# Revit family: for update_71130XXX_new
name_source: partatom
category: Plumbing Fixtures
revit_build: Autodesk Revit 2018 (Build: 20170223_1515(x64)
units: mm (PartAtom-declared; Revit-internal decimal feet)

## family parameters
Always vertical = No
Cut with Voids When Loaded = No
OmniClass Number = 23.31.11.00
OmniClass Title = Faucets
Part Type = Normal
Room Calculation Point = No
Round Connector Dimension = Use Diameter
Shared = No
Work Plane-Based = Yes

## types (1)
- 670 Matte Black
    Always visible = Yes
    BIMobject category = Taps & Mixers
    Connector Description = Water Inlet 9.5mm
    Default Elevation = 1219.2 mm  [stored 4 ft]
    Description = Logis Single lever basin mixer 210 with swivel spout and pop-up waste set
    Design country = Germany
    Diameter = 10 mm
    Edition number = 1
    IFC Classification = Valve
    Manufacturer = Hansgrohe
    Manufacturer country = Germany
    Manufacturer name = hansgrohe
    Masterformat 2014 Code = 22 41 39
    Masterformat 2014 Description = Residential Faucets, Supplies, and Trim
    Material 1 = Hansgrohe - Metal - 670 Matte Black
    Model = 71130XXX
    OmniClass Code = 23-31 11 00
    OmniClass Description = Faucets
    Product Guid = 0d3ea6d5-0a21-4000-b140-4378dfaab38f
    Product SKU = 71130XXX
    Product data url = https://bimobject.com
    Product family = Logis
    Product group = Basin mixers
    Product name = 71130XXX Logis Single lever basin mixer 210 with swivel spout and pop-up waste set
    Product url = https://www.hansgrohe.com
    QR code = https://bimobject.com
    UNSPSC Code = 301815
    URL = https://www.hansgrohe.com
    Uniclass 2015 Code = Pr_40_20_87
    Uniclass 2015 Name = Taps and water supply outlet fittings
    Uniformat II Code = D2010
    Uniformat II Description = Plumbing Fixtures
    Weight Net (Kg) = 1.5

note: [stored X ft] marks values corroborated as IEEE doubles in the binary element streams (Revit-internal decimal feet)

## geometry (parser evidence)
native form markers: Sweep x2
no freeform markers — native parametric forms only
